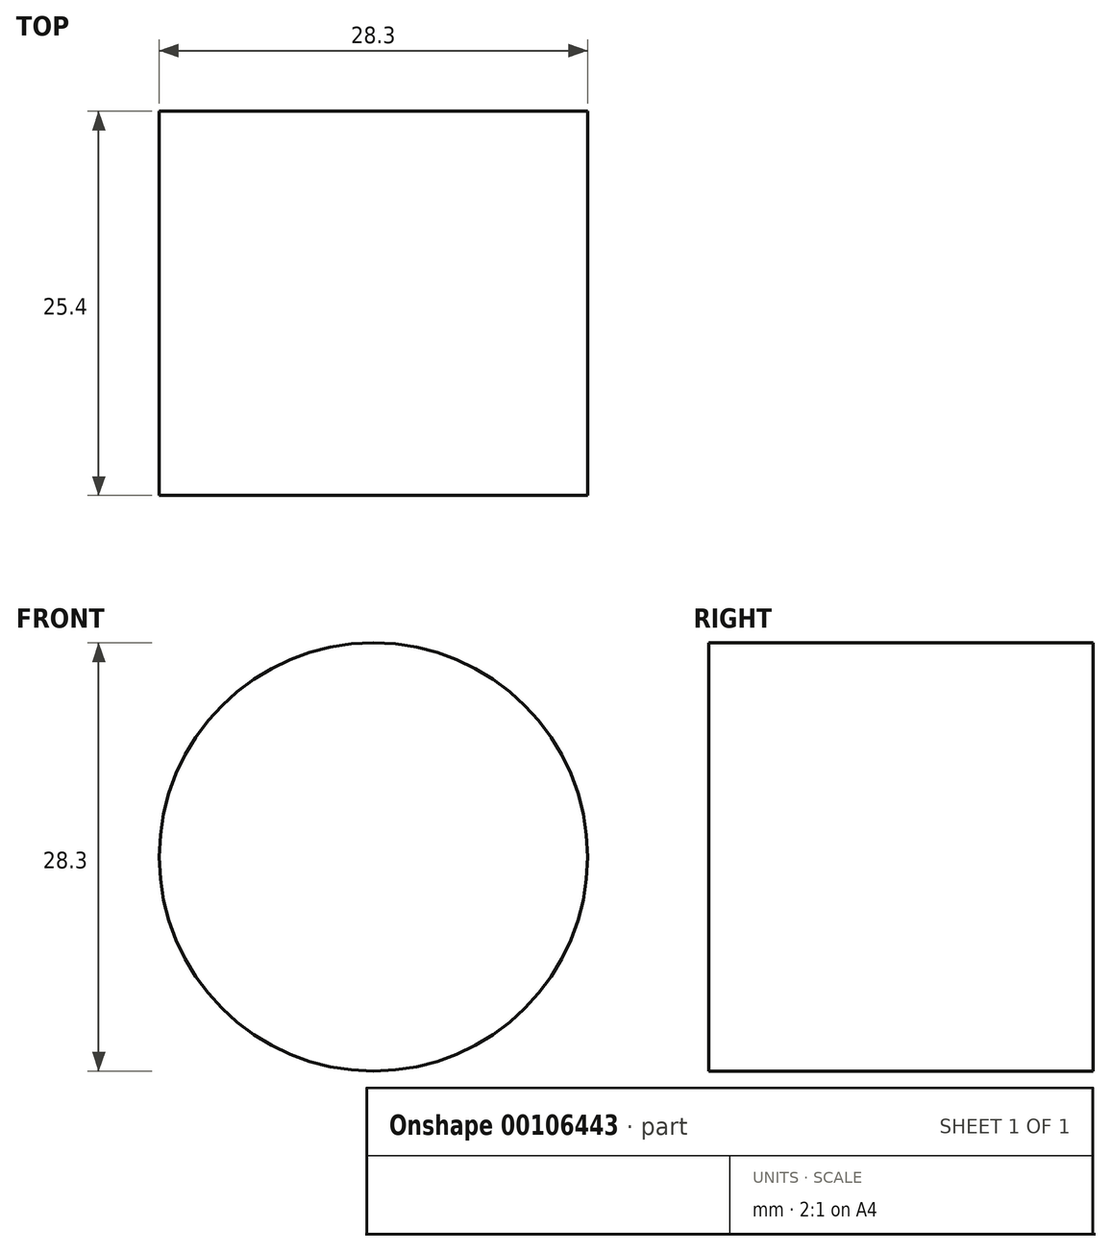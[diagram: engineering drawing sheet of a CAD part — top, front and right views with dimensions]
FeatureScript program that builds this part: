
annotation { "Feature Type Name" : "Feature", "Feature Type Description" : "" }
export const myFeature = defineFeature(function(context is Context, id is Id, definition is map)
    precondition{}
    {
        {
            var Q0;
            Q0=qCreatedBy(makeId("Front.planeOp"),FACE);
            var sketch = newSketch(context, id + "F0", { "sketchPlane" : qUnion([Q0])});
            skCircle(sketch, "E0", {"center": v(0, 0) * mm, "radius": 14.15 * mm});
            skSolve(sketch);
        }
        {
            var Q0;
            Q0 = qSketchRegion(id + "F0", true);
            extrude(context, id + "F1", {"entities" : qUnion([Q0]), "depth" : 25.4 * mm});
        }
    });
